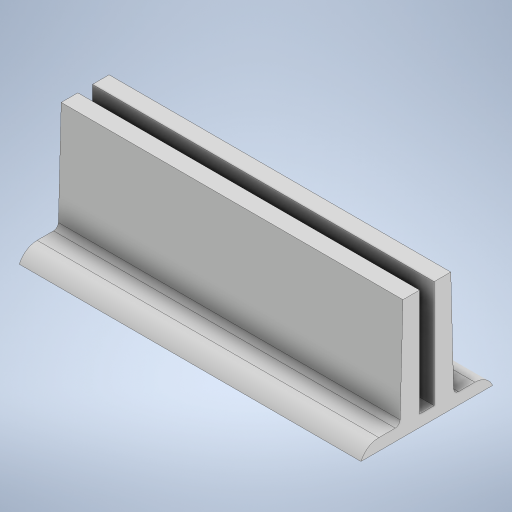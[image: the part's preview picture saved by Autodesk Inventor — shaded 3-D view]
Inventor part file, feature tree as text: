
AUTODESK INVENTOR PART (.ipt)
format: ipt  version: 2024 (Build 280153020, 153B)  size: 258,560 bytes
history: native  units: in
note: dims shown in document units (in); Inventor stores cm internally (conversion verified against a paired STEP export)
features: fillet x2, extrude x1, sketch x1
ambient origin geometry x8: Origin, YZ Plane, XZ Plane, XY Plane, X Axis, Y Axis, Z Axis, Center Point
bodies: Solid1 (feature_tree)
feature tree (4):
  extrude  "Extrusion1"  Depth=0.0295in
  fillet  "Fillet1"  Radius=0.4331in
  fillet  "Fillet2"  Radius=0.0669in
  sketch  "Sketch1"  dims[d0=0.0295in d1=0.0295in d2=0.4331in d3=0.0669in d4=0.4331in d5=0.0669in d6=0.0787in d7=0.0787in d8=0.1575in d9=0.1575in d10=90.0deg d11=0.0472in d12=1.378in d13=0.0in d14=0.0197in d15=0.0787in]
